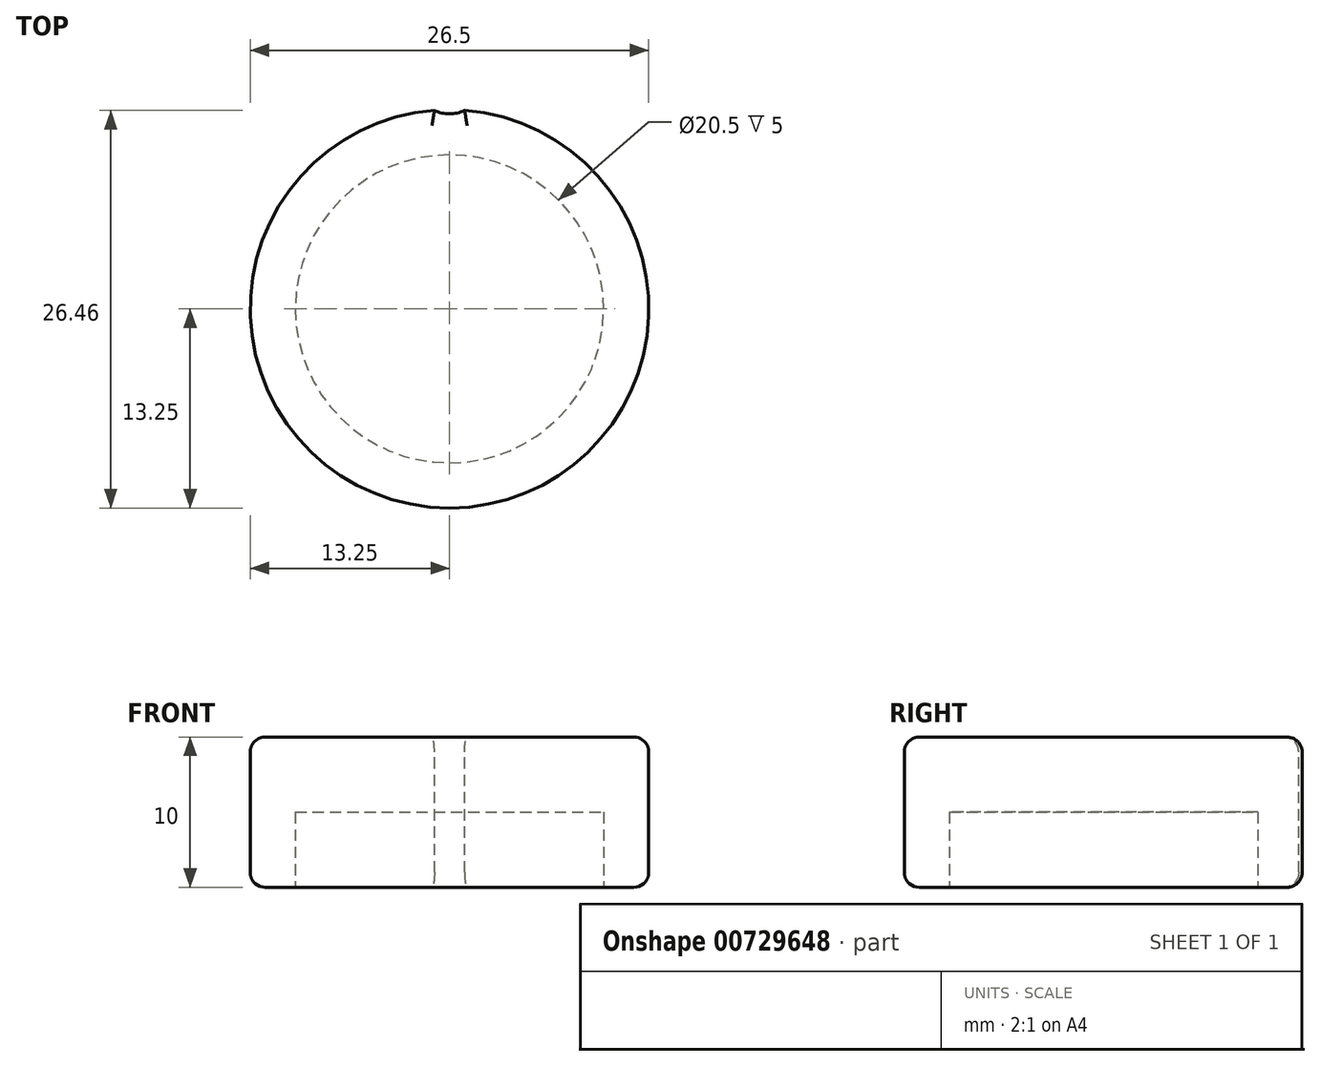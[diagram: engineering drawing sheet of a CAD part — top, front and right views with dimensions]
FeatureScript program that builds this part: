
annotation { "Feature Type Name" : "Feature", "Feature Type Description" : "" }
export const myFeature = defineFeature(function(context is Context, id is Id, definition is map)
    precondition{}
    {
        {
            var Q0;
            Q0=qCreatedBy(makeId("Top.planeOp"),FACE);
            var sketch = newSketch(context, id + "F0", { "sketchPlane" : qUnion([Q0])});
            skCircle(sketch, "E0", {"center": v(0, 0) * mm, "radius": 13.25 * mm});
            skLineSegment(sketch, "E1", {"start": v(0, 20.8) * mm, "end": v(0, -30.22) * mm, "construction": true});
            skSolve(sketch);
        }
        {
            var Q0;
            Q0 = qSketchRegion(id + "F0", true);
            extrude(context, id + "F1", {"entities" : qUnion([Q0]), "oppositeDirection" : true, "depth" : 10 * mm, "offsetDistance" : 25 * mm});
        }
        {
            var Q0;
            Q0=makeQuery(id+"F1.opExtrude","CAP_FACE",FACE,{"disambiguationData":[OSD([sQuery(id+"F0.wireOp",EDGE,"E0")])],"isStart":true});
            var sketch = newSketch(context, id + "F2", { "sketchPlane" : qUnion([Q0])});
            skCircle(sketch, "E2.converted", {"center": v(0, 15.25) * mm, "radius": 2.27 * mm});
            skPoint(sketch, "E3.orphan", {"position": v(-1, 13.21) * mm});
            skSolve(sketch);
        }
        {
            var Q0;
            {var subQ0=sQuery(id+"F2.wireOp",EDGE,"E2.converted");var subQ1=makeQuery(id+"F1.opExtrude","CAP_EDGE",EDGE,{"disambiguationData":[OSD([sQuery(id+"F0.wireOp",EDGE,"E0")])],"isStart":true});var subQ2=makeQuery(id+"F2.imprint","INTERSECT",VERTEX,{"disambiguationData":[OD(0.0)],"derivedFrom":[subQ1,subQ0]});Q0=makeQuery(id+"F2.imprint","IMPRINT",FACE,{"disambiguationData":[TD([[makeQuery(id+"F2.imprint","IMPRINT",EDGE,{"disambiguationData":[TD([[subQ2,1.0]])],"derivedFrom":subQ0}),1.0]])]});}
            var Q1;
            {var subQ0=sQuery(id+"F2.wireOp",EDGE,"E2.converted");var subQ1=makeQuery(id+"F1.opExtrude","CAP_EDGE",EDGE,{"disambiguationData":[OSD([sQuery(id+"F0.wireOp",EDGE,"E0")])],"isStart":true});var subQ2=makeQuery(id+"F2.imprint","INTERSECT",VERTEX,{"disambiguationData":[OD(0.0)],"derivedFrom":[subQ1,subQ0]});Q1=makeQuery(id+"F2.imprint","IMPRINT",FACE,{"disambiguationData":[TD([[makeQuery(id+"F2.imprint","IMPRINT",EDGE,{"disambiguationData":[TD([[subQ2,-1.0]])],"derivedFrom":subQ0}),1.0]])]});}
            extrude(context, id + "F3", {"entities" : qUnion([Q0, Q1]), "operationType" : NewBodyOperationType.REMOVE, "endBound" : BoundingType.THROUGH_ALL, "oppositeDirection" : true, "depth" : 25 * mm, "offsetDistance" : 25 * mm});
        }
        {
            var Q0;
            Q0=qCreatedBy(makeId("Front.planeOp"),FACE);
            var sketch = newSketch(context, id + "F4", { "sketchPlane" : qUnion([Q0])});
            skLineSegment(sketch, "E4", {"start": v(0, 47.36) * mm, "end": v(0, -51.3) * mm, "construction": true});
            skSolve(sketch);
        }
        {
            var Q0;
            Q0=makeQuery(id+"F1.opExtrude","CAP_FACE",FACE,{"disambiguationData":[OSD([sQuery(id+"F0.wireOp",EDGE,"E0")])],"isStart":true});
            var Q1;
            Q1=makeQuery(id+"F1.opExtrude","CAP_FACE",FACE,{"disambiguationData":[OSD([sQuery(id+"F0.wireOp",EDGE,"E0")])],"isStart":false});
            fillet(context, id + "F5", {"entities" : qUnion([Q0, Q1]), "radius" : 1 * mm, "tangentPropagation" : true, "allowEdgeOverflow" : false});
        }
        {
            var Q0;
            Q0=makeQuery(id+"F1.opExtrude","CAP_FACE",FACE,{"disambiguationData":[OSD([sQuery(id+"F0.wireOp",EDGE,"E0")])],"isStart":false});
            var sketch = newSketch(context, id + "F6", { "sketchPlane" : qUnion([Q0])});
            skCircle(sketch, "E5", {"center": v(0, 0) * mm, "radius": 10.25 * mm});
            skSolve(sketch);
        }
        {
            var Q0;
            Q0=makeQuery(id+"F6.imprint","IMPRINT",FACE,{"disambiguationData":[TD([[makeQuery(id+"F6.imprint","IMPRINT",EDGE,{"derivedFrom":sQuery(id+"F6.wireOp",EDGE,"E5")}),1.0]])]});
            extrude(context, id + "F7", {"entities" : qUnion([Q0]), "operationType" : NewBodyOperationType.REMOVE, "oppositeDirection" : true, "depth" : 5 * mm, "offsetDistance" : 25 * mm});
        }
    });
